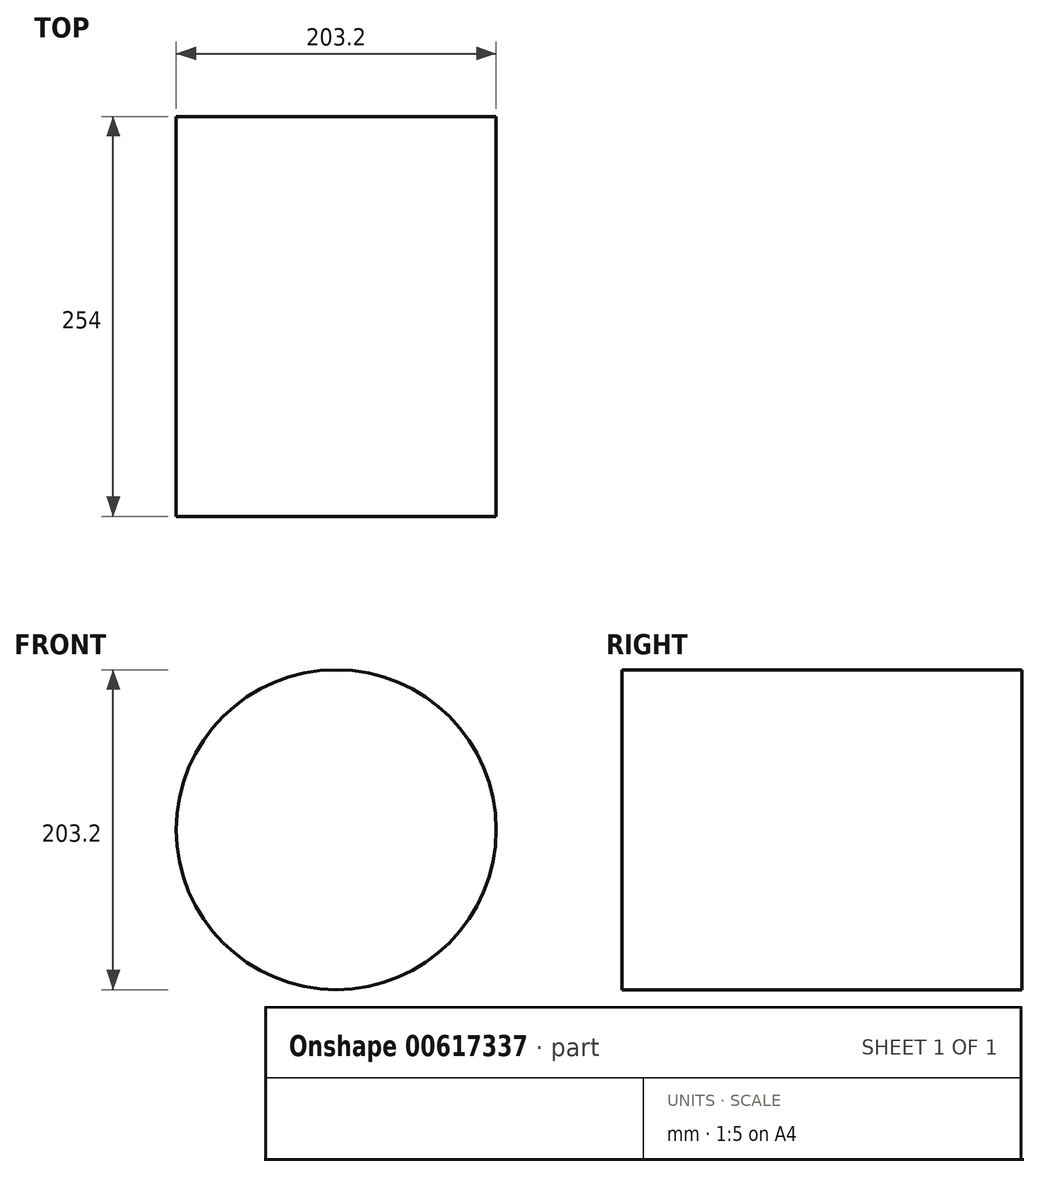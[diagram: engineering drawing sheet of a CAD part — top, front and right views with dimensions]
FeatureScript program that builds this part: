
annotation { "Feature Type Name" : "Feature", "Feature Type Description" : "" }
export const myFeature = defineFeature(function(context is Context, id is Id, definition is map)
    precondition{}
    {
        {
            var Q0;
            Q0=qCreatedBy(makeId("Front.planeOp"),FACE);
            var sketch = newSketch(context, id + "F0", { "sketchPlane" : qUnion([Q0])});
            skCircle(sketch, "E0", {"center": v(-9, 14.7) * mm, "radius": 101.6 * mm});
            skSolve(sketch);
        }
        {
            var Q0;
            Q0 = qSketchRegion(id + "F0", true);
            extrude(context, id + "F1", {"entities" : qUnion([Q0]), "depth" : 254 * mm, "offsetDistance" : 25.4 * mm});
        }
    });
